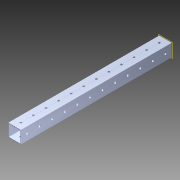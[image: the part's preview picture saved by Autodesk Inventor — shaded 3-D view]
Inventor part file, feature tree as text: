
AUTODESK INVENTOR PART (.ipt)
format: ipt  version: 2014 (Build 180170000, 170)  size: 1,148,416 bytes
history: native  units: in
note: dims shown in document units (in); Inventor stores cm internally (conversion verified against a paired STEP export)
features: pattern_circular x1, other x1, plane x1, extrude x1, imported_body x1, sketch x1
ambient origin geometry x8: Origin, YZ Plane, XZ Plane, XY Plane, X Axis, Y Axis, Z Axis, Center Point
bodies: Body1 (feature_tree)
feature tree (6):
  pattern_circular  "CirPattern2"
  other  "217-3426-STEP1"
  plane  "Work Plane1"
  extrude  "Extrusion1"  Depth=3937.0079in TaperAngle=0.0deg
  imported_body  "Base1"
  sketch  "Sketch1"  dims[d0=-7.0in d1=3937.0079in d2=0.0in]
